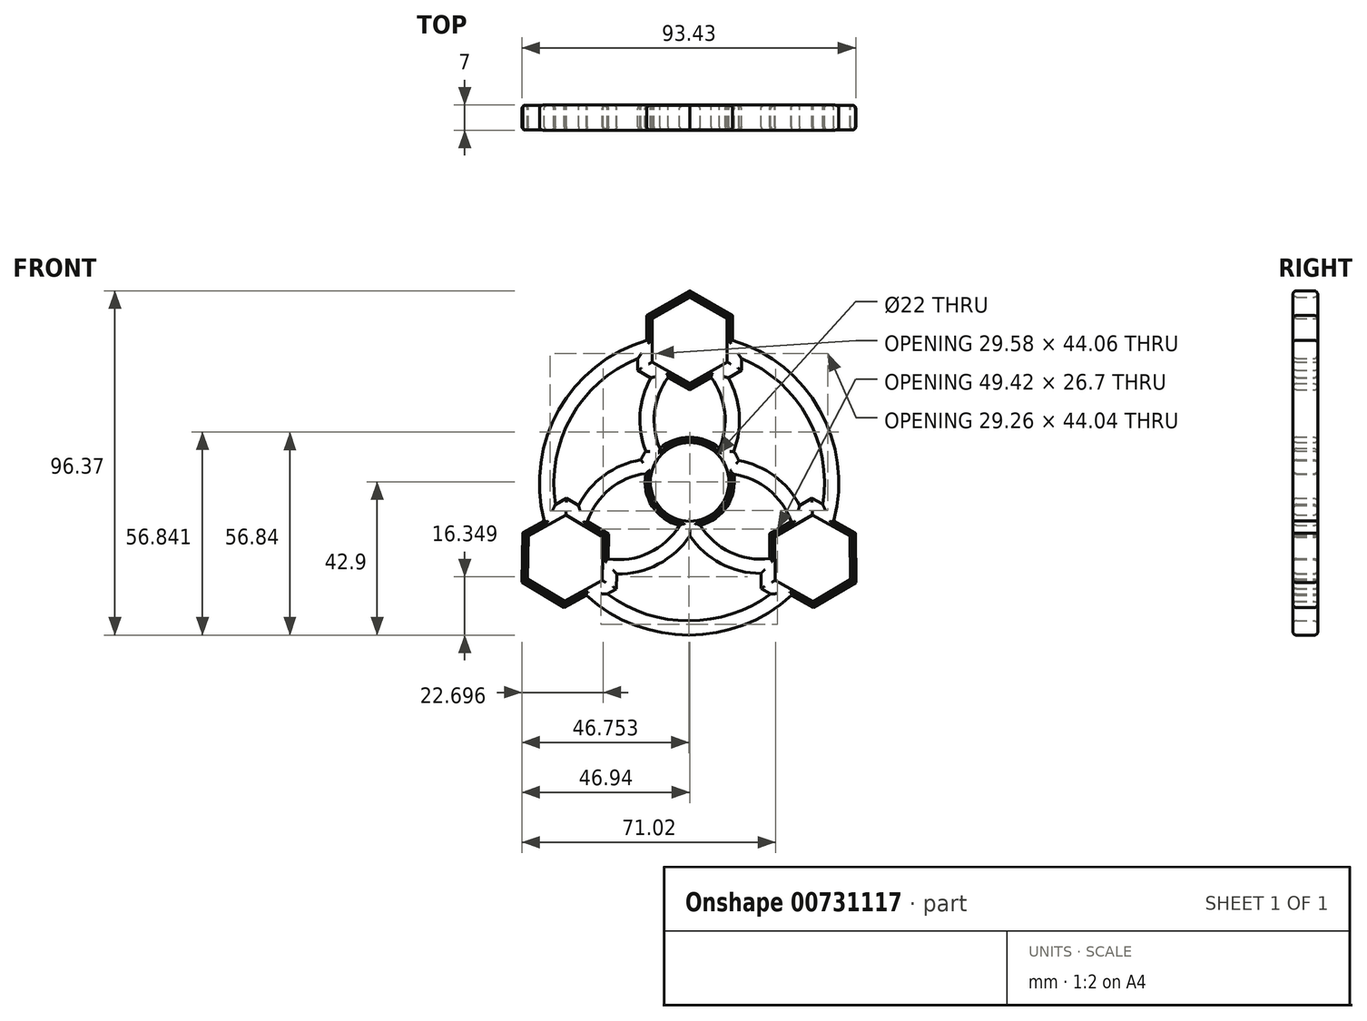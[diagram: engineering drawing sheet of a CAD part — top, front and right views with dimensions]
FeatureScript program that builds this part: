
annotation { "Feature Type Name" : "Feature", "Feature Type Description" : "" }
export const myFeature = defineFeature(function(context is Context, id is Id, definition is map)
    precondition{}
    {
        {
            var Q0;
            Q0=qCreatedBy(makeId("Front.planeOp"),FACE);
            var sketch = newSketch(context, id + "F0", { "sketchPlane" : qUnion([Q0])});
            skCircle(sketch, "E0", {"center": v(0, 0) * mm, "radius": 11 * mm});
            skCircle(sketch, "E1", {"center": v(0, 0) * mm, "radius": 12.5 * mm});
            skCircle(sketch, "E2.cCircle", {"center": v(0, 39.61) * mm, "radius": 10.5 * mm, "construction": true});
            skLineSegment(sketch, "E2.0", {"start": v(10.5, 45.68) * mm, "end": v(10.5, 33.55) * mm});
            skLineSegment(sketch, "E2.1", {"start": v(10.5, 33.55) * mm, "end": v(0, 27.5) * mm});
            skLineSegment(sketch, "E2.2", {"start": v(0, 27.5) * mm, "end": v(-10.5, 33.55) * mm});
            skLineSegment(sketch, "E2.3", {"start": v(-10.5, 33.55) * mm, "end": v(-10.5, 45.68) * mm});
            skLineSegment(sketch, "E2.4", {"start": v(-10.5, 45.68) * mm, "end": v(0, 51.74) * mm});
            skLineSegment(sketch, "E2.5", {"start": v(0, 51.74) * mm, "end": v(10.5, 45.68) * mm});
            skPoint(sketch, "E2.0.midPoint", {"position": v(10.5, 39.61) * mm});
            skCircle(sketch, "E3.cCircle", {"center": v(-34.82, -21.35) * mm, "radius": 10.5 * mm, "construction": true});
            skLineSegment(sketch, "E3.0", {"start": v(-24.2, -15.49) * mm, "end": v(-24.43, -27.61) * mm});
            skLineSegment(sketch, "E3.1", {"start": v(-24.43, -27.61) * mm, "end": v(-35.04, -33.48) * mm});
            skLineSegment(sketch, "E3.2", {"start": v(-35.04, -33.48) * mm, "end": v(-45.43, -27.22) * mm});
            skLineSegment(sketch, "E3.3", {"start": v(-45.43, -27.22) * mm, "end": v(-45.2, -15.1) * mm});
            skLineSegment(sketch, "E3.4", {"start": v(-45.2, -15.1) * mm, "end": v(-34.59, -9.23) * mm});
            skLineSegment(sketch, "E3.5", {"start": v(-34.59, -9.23) * mm, "end": v(-24.2, -15.49) * mm});
            skPoint(sketch, "E3.0.midPoint", {"position": v(-24.32, -21.55) * mm});
            skCircle(sketch, "E4.cCircle", {"center": v(34.42, -21.36) * mm, "radius": 10.5 * mm, "construction": true});
            skLineSegment(sketch, "E4.0", {"start": v(34.54, -33.48) * mm, "end": v(23.98, -27.52) * mm});
            skLineSegment(sketch, "E4.1", {"start": v(23.98, -27.52) * mm, "end": v(23.86, -15.4) * mm});
            skLineSegment(sketch, "E4.2", {"start": v(23.86, -15.4) * mm, "end": v(34.3, -9.23) * mm});
            skLineSegment(sketch, "E4.3", {"start": v(34.3, -9.23) * mm, "end": v(44.85, -15.19) * mm});
            skLineSegment(sketch, "E4.4", {"start": v(44.85, -15.19) * mm, "end": v(44.98, -27.31) * mm});
            skLineSegment(sketch, "E4.5", {"start": v(44.98, -27.31) * mm, "end": v(34.54, -33.48) * mm});
            skPoint(sketch, "E4.0.midPoint", {"position": v(29.26, -30.5) * mm});
            skCircle(sketch, "E5.cCircle", {"center": v(0, 39.61) * mm, "radius": 12 * mm, "construction": true});
            skLineSegment(sketch, "E5.0", {"start": v(12, 46.54) * mm, "end": v(12, 32.69) * mm});
            skLineSegment(sketch, "E5.1", {"start": v(12, 32.69) * mm, "end": v(0, 25.76) * mm});
            skLineSegment(sketch, "E5.2", {"start": v(0, 25.76) * mm, "end": v(-12, 32.69) * mm});
            skLineSegment(sketch, "E5.3", {"start": v(-12, 32.69) * mm, "end": v(-12, 46.54) * mm});
            skLineSegment(sketch, "E5.4", {"start": v(-12, 46.54) * mm, "end": v(0, 53.47) * mm});
            skLineSegment(sketch, "E5.5", {"start": v(0, 53.47) * mm, "end": v(12, 46.54) * mm});
            skPoint(sketch, "E5.0.midPoint", {"position": v(12, 39.61) * mm});
            skCircle(sketch, "E6.cCircle", {"center": v(34.42, -21.36) * mm, "radius": 12 * mm, "construction": true});
            skLineSegment(sketch, "E6.0", {"start": v(34.27, -7.5) * mm, "end": v(46.34, -14.3) * mm});
            skLineSegment(sketch, "E6.1", {"start": v(46.34, -14.3) * mm, "end": v(46.49, -28.16) * mm});
            skLineSegment(sketch, "E6.2", {"start": v(46.49, -28.16) * mm, "end": v(34.56, -35.21) * mm});
            skLineSegment(sketch, "E6.3", {"start": v(34.56, -35.21) * mm, "end": v(22.49, -28.4) * mm});
            skLineSegment(sketch, "E6.4", {"start": v(22.49, -28.4) * mm, "end": v(22.34, -14.55) * mm});
            skLineSegment(sketch, "E6.5", {"start": v(22.34, -14.55) * mm, "end": v(34.27, -7.5) * mm});
            skPoint(sketch, "E6.0.midPoint", {"position": v(40.3, -10.9) * mm});
            skCircle(sketch, "E7.cCircle", {"center": v(-34.82, -21.35) * mm, "radius": 12 * mm, "construction": true});
            skLineSegment(sketch, "E7.0", {"start": v(-34.56, -7.5) * mm, "end": v(-22.69, -14.65) * mm});
            skLineSegment(sketch, "E7.1", {"start": v(-22.69, -14.65) * mm, "end": v(-22.95, -28.5) * mm});
            skLineSegment(sketch, "E7.2", {"start": v(-22.95, -28.5) * mm, "end": v(-35.07, -35.2) * mm});
            skLineSegment(sketch, "E7.3", {"start": v(-35.07, -35.2) * mm, "end": v(-46.94, -28.06) * mm});
            skLineSegment(sketch, "E7.4", {"start": v(-46.94, -28.06) * mm, "end": v(-46.68, -14.2) * mm});
            skLineSegment(sketch, "E7.5", {"start": v(-46.68, -14.2) * mm, "end": v(-34.56, -7.5) * mm});
            skPoint(sketch, "E7.0.midPoint", {"position": v(-28.62, -11.08) * mm});
            skArc(sketch, "E8", {"start": v(40.3, -10.9) * mm, "mid": v(36.42, 20.11) * mm, "end": v(12, 39.61) * mm});
            skArc(sketch, "E9", {"start": v(-12, 39.61) * mm, "mid": v(-36.59, 20.17) * mm, "end": v(-40.71, -10.9) * mm});
            skArc(sketch, "E10", {"start": v(-28.93, -31.8) * mm, "mid": v(-0.2, -42.9) * mm, "end": v(28.52, -31.8) * mm});
            skPoint(sketch, "E10.startSnap0", {"position": v(28.52, -31.8) * mm});
            skArc(sketch, "E11", {"start": v(0, 0) * mm, "mid": v(9.54, 13.27) * mm, "end": v(6, 29.22) * mm});
            skArc(sketch, "E12", {"start": v(-6, 29.22) * mm, "mid": v(-9.54, 13.27) * mm, "end": v(0, 0) * mm});
            skArc(sketch, "E13", {"start": v(0, 0) * mm, "mid": v(-16.9, 1.15) * mm, "end": v(-28.62, -11.08) * mm});
            skArc(sketch, "E14", {"start": v(-22.82, -21.58) * mm, "mid": v(-6.18, -16.32) * mm, "end": v(0, 0) * mm});
            skArc(sketch, "E15", {"start": v(28.3, -11.03) * mm, "mid": v(16.7, 1) * mm, "end": v(0, 0) * mm});
            skArc(sketch, "E16", {"start": v(0, 0) * mm, "mid": v(6.1, -16.08) * mm, "end": v(22.42, -21.48) * mm});
            skSolve(sketch);
        }
        {
            var Q0;
            Q0 = qSketchRegion(id + "F0", true);
            var Q1;
            {var subQ0=sQuery(id+"F0.wireOp",EDGE,"E11");var subQ1=sQuery(id+"F0.wireOp",EDGE,"E0");var subQ2=makeQuery(id+"F0.imprint","INTERSECT",VERTEX,{"derivedFrom":[subQ1,subQ0]});Q1=makeQuery(id+"F0.imprint","IMPRINT",FACE,{"disambiguationData":[TD([[makeQuery(id+"F0.imprint","IMPRINT",EDGE,{"disambiguationData":[TD([[subQ2,-1.0]])],"derivedFrom":subQ1}),-1.0]])]});}
            var Q2;
            {var subQ0=sQuery(id+"F0.wireOp",EDGE,"E12");var subQ1=sQuery(id+"F0.wireOp",EDGE,"E0");var subQ2=makeQuery(id+"F0.imprint","INTERSECT",VERTEX,{"derivedFrom":[subQ1,subQ0]});Q2=makeQuery(id+"F0.imprint","IMPRINT",FACE,{"disambiguationData":[TD([[makeQuery(id+"F0.imprint","IMPRINT",EDGE,{"disambiguationData":[TD([[subQ2,-1.0]])],"derivedFrom":subQ1}),-1.0]])]});}
            var Q3;
            {var subQ0=sQuery(id+"F0.wireOp",EDGE,"E13");var subQ1=sQuery(id+"F0.wireOp",EDGE,"E0");var subQ2=makeQuery(id+"F0.imprint","INTERSECT",VERTEX,{"derivedFrom":[subQ1,subQ0]});Q3=makeQuery(id+"F0.imprint","IMPRINT",FACE,{"disambiguationData":[TD([[makeQuery(id+"F0.imprint","IMPRINT",EDGE,{"disambiguationData":[TD([[subQ2,-1.0]])],"derivedFrom":subQ1}),-1.0]])]});}
            var Q4;
            {var subQ0=sQuery(id+"F0.wireOp",EDGE,"E14");var subQ1=sQuery(id+"F0.wireOp",EDGE,"E0");var subQ2=makeQuery(id+"F0.imprint","INTERSECT",VERTEX,{"derivedFrom":[subQ1,subQ0]});Q4=makeQuery(id+"F0.imprint","IMPRINT",FACE,{"disambiguationData":[TD([[makeQuery(id+"F0.imprint","IMPRINT",EDGE,{"disambiguationData":[TD([[subQ2,-1.0]])],"derivedFrom":subQ1}),-1.0]])]});}
            var Q5;
            {var subQ0=sQuery(id+"F0.wireOp",EDGE,"E15");var subQ1=sQuery(id+"F0.wireOp",EDGE,"E0");var subQ2=makeQuery(id+"F0.imprint","INTERSECT",VERTEX,{"derivedFrom":[subQ1,subQ0]});Q5=makeQuery(id+"F0.imprint","IMPRINT",FACE,{"disambiguationData":[TD([[makeQuery(id+"F0.imprint","IMPRINT",EDGE,{"disambiguationData":[TD([[subQ2,1.0]])],"derivedFrom":subQ1}),-1.0]])]});}
            var Q6;
            {var subQ0=sQuery(id+"F0.wireOp",EDGE,"E11");var subQ1=sQuery(id+"F0.wireOp",EDGE,"E0");var subQ2=makeQuery(id+"F0.imprint","INTERSECT",VERTEX,{"derivedFrom":[subQ1,subQ0]});Q6=makeQuery(id+"F0.imprint","IMPRINT",FACE,{"disambiguationData":[TD([[makeQuery(id+"F0.imprint","IMPRINT",EDGE,{"disambiguationData":[TD([[subQ2,1.0]])],"derivedFrom":subQ1}),-1.0]])]});}
            extrude(context, id + "F1", {"entities" : qUnion([Q0, Q1, Q2, Q3, Q4, Q5, Q6]), "endBound" : BoundingType.SYMMETRIC, "depth" : 7 * mm, "offsetDistance" : 25 * mm});
        }
        {
            var Q0;
            Q0=makeQuery(id+"F1.opExtrude","CAP_FACE",FACE,{"disambiguationData":[OSD([sQuery(id+"F0.wireOp",EDGE,"E0"),sQuery(id+"F0.wireOp",EDGE,"E1"),sQuery(id+"F0.wireOp",EDGE,"E2.0"),sQuery(id+"F0.wireOp",EDGE,"E2.1"),sQuery(id+"F0.wireOp",EDGE,"E2.2"),sQuery(id+"F0.wireOp",EDGE,"E2.3"),sQuery(id+"F0.wireOp",EDGE,"E2.4"),sQuery(id+"F0.wireOp",EDGE,"E2.5"),sQuery(id+"F0.wireOp",EDGE,"E3.0"),sQuery(id+"F0.wireOp",EDGE,"E3.1"),sQuery(id+"F0.wireOp",EDGE,"E3.2"),sQuery(id+"F0.wireOp",EDGE,"E3.3"),sQuery(id+"F0.wireOp",EDGE,"E3.4"),sQuery(id+"F0.wireOp",EDGE,"E3.5"),sQuery(id+"F0.wireOp",EDGE,"E4.0"),sQuery(id+"F0.wireOp",EDGE,"E4.1"),sQuery(id+"F0.wireOp",EDGE,"E4.2"),sQuery(id+"F0.wireOp",EDGE,"E4.3"),sQuery(id+"F0.wireOp",EDGE,"E4.4"),sQuery(id+"F0.wireOp",EDGE,"E4.5"),sQuery(id+"F0.wireOp",EDGE,"E5.0"),sQuery(id+"F0.wireOp",EDGE,"E5.1"),sQuery(id+"F0.wireOp",EDGE,"E5.2"),sQuery(id+"F0.wireOp",EDGE,"E5.3"),sQuery(id+"F0.wireOp",EDGE,"E5.4"),sQuery(id+"F0.wireOp",EDGE,"E5.5"),sQuery(id+"F0.wireOp",EDGE,"E6.0"),sQuery(id+"F0.wireOp",EDGE,"E6.1"),sQuery(id+"F0.wireOp",EDGE,"E6.2"),sQuery(id+"F0.wireOp",EDGE,"E6.3"),sQuery(id+"F0.wireOp",EDGE,"E6.4"),sQuery(id+"F0.wireOp",EDGE,"E6.5"),sQuery(id+"F0.wireOp",EDGE,"E7.0"),sQuery(id+"F0.wireOp",EDGE,"E7.1"),sQuery(id+"F0.wireOp",EDGE,"E7.2"),sQuery(id+"F0.wireOp",EDGE,"E7.3"),sQuery(id+"F0.wireOp",EDGE,"E7.4"),sQuery(id+"F0.wireOp",EDGE,"E7.5"),sQuery(id+"F0.wireOp",EDGE,"E8"),sQuery(id+"F0.wireOp",EDGE,"E9"),sQuery(id+"F0.wireOp",EDGE,"E10"),sQuery(id+"F0.wireOp",EDGE,"E11"),sQuery(id+"F0.wireOp",EDGE,"E12"),sQuery(id+"F0.wireOp",EDGE,"E13"),sQuery(id+"F0.wireOp",EDGE,"E14"),sQuery(id+"F0.wireOp",EDGE,"E15"),sQuery(id+"F0.wireOp",EDGE,"E16")])],"isStart":false});
            var Q1;
            Q1=makeQuery(id+"F1.opExtrude","CAP_FACE",FACE,{"disambiguationData":[OSD([sQuery(id+"F0.wireOp",EDGE,"E0"),sQuery(id+"F0.wireOp",EDGE,"E1"),sQuery(id+"F0.wireOp",EDGE,"E2.0"),sQuery(id+"F0.wireOp",EDGE,"E2.1"),sQuery(id+"F0.wireOp",EDGE,"E2.2"),sQuery(id+"F0.wireOp",EDGE,"E2.3"),sQuery(id+"F0.wireOp",EDGE,"E2.4"),sQuery(id+"F0.wireOp",EDGE,"E2.5"),sQuery(id+"F0.wireOp",EDGE,"E3.0"),sQuery(id+"F0.wireOp",EDGE,"E3.1"),sQuery(id+"F0.wireOp",EDGE,"E3.2"),sQuery(id+"F0.wireOp",EDGE,"E3.3"),sQuery(id+"F0.wireOp",EDGE,"E3.4"),sQuery(id+"F0.wireOp",EDGE,"E3.5"),sQuery(id+"F0.wireOp",EDGE,"E4.0"),sQuery(id+"F0.wireOp",EDGE,"E4.1"),sQuery(id+"F0.wireOp",EDGE,"E4.2"),sQuery(id+"F0.wireOp",EDGE,"E4.3"),sQuery(id+"F0.wireOp",EDGE,"E4.4"),sQuery(id+"F0.wireOp",EDGE,"E4.5"),sQuery(id+"F0.wireOp",EDGE,"E5.0"),sQuery(id+"F0.wireOp",EDGE,"E5.1"),sQuery(id+"F0.wireOp",EDGE,"E5.2"),sQuery(id+"F0.wireOp",EDGE,"E5.3"),sQuery(id+"F0.wireOp",EDGE,"E5.4"),sQuery(id+"F0.wireOp",EDGE,"E5.5"),sQuery(id+"F0.wireOp",EDGE,"E6.0"),sQuery(id+"F0.wireOp",EDGE,"E6.1"),sQuery(id+"F0.wireOp",EDGE,"E6.2"),sQuery(id+"F0.wireOp",EDGE,"E6.3"),sQuery(id+"F0.wireOp",EDGE,"E6.4"),sQuery(id+"F0.wireOp",EDGE,"E6.5"),sQuery(id+"F0.wireOp",EDGE,"E7.0"),sQuery(id+"F0.wireOp",EDGE,"E7.1"),sQuery(id+"F0.wireOp",EDGE,"E7.2"),sQuery(id+"F0.wireOp",EDGE,"E7.3"),sQuery(id+"F0.wireOp",EDGE,"E7.4"),sQuery(id+"F0.wireOp",EDGE,"E7.5"),sQuery(id+"F0.wireOp",EDGE,"E8"),sQuery(id+"F0.wireOp",EDGE,"E9"),sQuery(id+"F0.wireOp",EDGE,"E10"),sQuery(id+"F0.wireOp",EDGE,"E11"),sQuery(id+"F0.wireOp",EDGE,"E12"),sQuery(id+"F0.wireOp",EDGE,"E13"),sQuery(id+"F0.wireOp",EDGE,"E14"),sQuery(id+"F0.wireOp",EDGE,"E15"),sQuery(id+"F0.wireOp",EDGE,"E16")])],"isStart":true});
            shell(context, id + "F2", {"entities" : qUnion([Q0, Q1]), "thickness" : 4 * mm});
        }
        {
            var Q0;
            Q0=makeQuery(id+"F1.opExtrude","CAP_FACE",FACE,{"disambiguationData":[OSD([sQuery(id+"F0.wireOp",EDGE,"E0"),sQuery(id+"F0.wireOp",EDGE,"E1"),sQuery(id+"F0.wireOp",EDGE,"E2.0"),sQuery(id+"F0.wireOp",EDGE,"E2.1"),sQuery(id+"F0.wireOp",EDGE,"E2.2"),sQuery(id+"F0.wireOp",EDGE,"E2.3"),sQuery(id+"F0.wireOp",EDGE,"E2.4"),sQuery(id+"F0.wireOp",EDGE,"E2.5"),sQuery(id+"F0.wireOp",EDGE,"E3.0"),sQuery(id+"F0.wireOp",EDGE,"E3.1"),sQuery(id+"F0.wireOp",EDGE,"E3.2"),sQuery(id+"F0.wireOp",EDGE,"E3.3"),sQuery(id+"F0.wireOp",EDGE,"E3.4"),sQuery(id+"F0.wireOp",EDGE,"E3.5"),sQuery(id+"F0.wireOp",EDGE,"E4.0"),sQuery(id+"F0.wireOp",EDGE,"E4.1"),sQuery(id+"F0.wireOp",EDGE,"E4.2"),sQuery(id+"F0.wireOp",EDGE,"E4.3"),sQuery(id+"F0.wireOp",EDGE,"E4.4"),sQuery(id+"F0.wireOp",EDGE,"E4.5"),sQuery(id+"F0.wireOp",EDGE,"E5.0"),sQuery(id+"F0.wireOp",EDGE,"E5.1"),sQuery(id+"F0.wireOp",EDGE,"E5.2"),sQuery(id+"F0.wireOp",EDGE,"E5.3"),sQuery(id+"F0.wireOp",EDGE,"E5.4"),sQuery(id+"F0.wireOp",EDGE,"E5.5"),sQuery(id+"F0.wireOp",EDGE,"E6.0"),sQuery(id+"F0.wireOp",EDGE,"E6.1"),sQuery(id+"F0.wireOp",EDGE,"E6.2"),sQuery(id+"F0.wireOp",EDGE,"E6.3"),sQuery(id+"F0.wireOp",EDGE,"E6.4"),sQuery(id+"F0.wireOp",EDGE,"E6.5"),sQuery(id+"F0.wireOp",EDGE,"E7.0"),sQuery(id+"F0.wireOp",EDGE,"E7.1"),sQuery(id+"F0.wireOp",EDGE,"E7.2"),sQuery(id+"F0.wireOp",EDGE,"E7.3"),sQuery(id+"F0.wireOp",EDGE,"E7.4"),sQuery(id+"F0.wireOp",EDGE,"E7.5"),sQuery(id+"F0.wireOp",EDGE,"E8"),sQuery(id+"F0.wireOp",EDGE,"E9"),sQuery(id+"F0.wireOp",EDGE,"E10"),sQuery(id+"F0.wireOp",EDGE,"E11"),sQuery(id+"F0.wireOp",EDGE,"E12"),sQuery(id+"F0.wireOp",EDGE,"E13"),sQuery(id+"F0.wireOp",EDGE,"E14"),sQuery(id+"F0.wireOp",EDGE,"E15"),sQuery(id+"F0.wireOp",EDGE,"E16")])],"isStart":false});
            fillet(context, id + "F3", {"entities" : qUnion([Q0]), "radius" : 1 * mm, "tangentPropagation" : true, "allowEdgeOverflow" : false});
        }
        {
            var Q0;
            Q0=makeQuery(id+"F1.opExtrude","CAP_FACE",FACE,{"disambiguationData":[OSD([sQuery(id+"F0.wireOp",EDGE,"E0"),sQuery(id+"F0.wireOp",EDGE,"E1"),sQuery(id+"F0.wireOp",EDGE,"E2.0"),sQuery(id+"F0.wireOp",EDGE,"E2.1"),sQuery(id+"F0.wireOp",EDGE,"E2.2"),sQuery(id+"F0.wireOp",EDGE,"E2.3"),sQuery(id+"F0.wireOp",EDGE,"E2.4"),sQuery(id+"F0.wireOp",EDGE,"E2.5"),sQuery(id+"F0.wireOp",EDGE,"E3.0"),sQuery(id+"F0.wireOp",EDGE,"E3.1"),sQuery(id+"F0.wireOp",EDGE,"E3.2"),sQuery(id+"F0.wireOp",EDGE,"E3.3"),sQuery(id+"F0.wireOp",EDGE,"E3.4"),sQuery(id+"F0.wireOp",EDGE,"E3.5"),sQuery(id+"F0.wireOp",EDGE,"E4.0"),sQuery(id+"F0.wireOp",EDGE,"E4.1"),sQuery(id+"F0.wireOp",EDGE,"E4.2"),sQuery(id+"F0.wireOp",EDGE,"E4.3"),sQuery(id+"F0.wireOp",EDGE,"E4.4"),sQuery(id+"F0.wireOp",EDGE,"E4.5"),sQuery(id+"F0.wireOp",EDGE,"E5.0"),sQuery(id+"F0.wireOp",EDGE,"E5.1"),sQuery(id+"F0.wireOp",EDGE,"E5.2"),sQuery(id+"F0.wireOp",EDGE,"E5.3"),sQuery(id+"F0.wireOp",EDGE,"E5.4"),sQuery(id+"F0.wireOp",EDGE,"E5.5"),sQuery(id+"F0.wireOp",EDGE,"E6.0"),sQuery(id+"F0.wireOp",EDGE,"E6.1"),sQuery(id+"F0.wireOp",EDGE,"E6.2"),sQuery(id+"F0.wireOp",EDGE,"E6.3"),sQuery(id+"F0.wireOp",EDGE,"E6.4"),sQuery(id+"F0.wireOp",EDGE,"E6.5"),sQuery(id+"F0.wireOp",EDGE,"E7.0"),sQuery(id+"F0.wireOp",EDGE,"E7.1"),sQuery(id+"F0.wireOp",EDGE,"E7.2"),sQuery(id+"F0.wireOp",EDGE,"E7.3"),sQuery(id+"F0.wireOp",EDGE,"E7.4"),sQuery(id+"F0.wireOp",EDGE,"E7.5"),sQuery(id+"F0.wireOp",EDGE,"E8"),sQuery(id+"F0.wireOp",EDGE,"E9"),sQuery(id+"F0.wireOp",EDGE,"E10"),sQuery(id+"F0.wireOp",EDGE,"E11"),sQuery(id+"F0.wireOp",EDGE,"E12"),sQuery(id+"F0.wireOp",EDGE,"E13"),sQuery(id+"F0.wireOp",EDGE,"E14"),sQuery(id+"F0.wireOp",EDGE,"E15"),sQuery(id+"F0.wireOp",EDGE,"E16")])],"isStart":true});
            fillet(context, id + "F4", {"entities" : qUnion([Q0]), "radius" : 1 * mm, "tangentPropagation" : true, "allowEdgeOverflow" : false});
        }
    });
